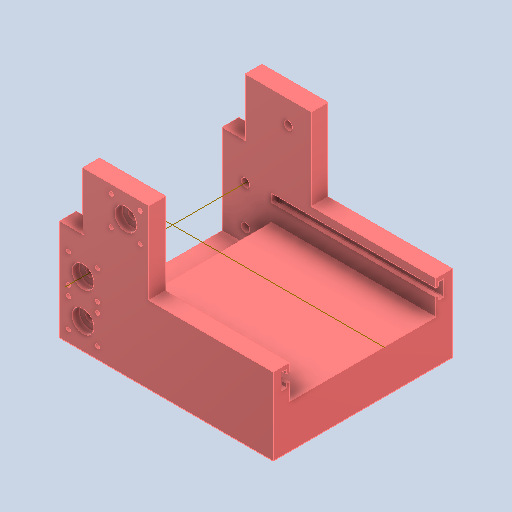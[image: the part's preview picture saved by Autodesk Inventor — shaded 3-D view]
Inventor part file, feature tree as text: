
AUTODESK INVENTOR PART (.ipt)
format: ipt  version: 2025 (Build 290162000, 162)  size: 441,344 bytes
history: native  units: mm
features: extrude x7, sketch x7, other x4, fillet x2, mirror x1, projected_geometry x1
ambient origin geometry x8: Origin, YZ Plane, XZ Plane, XY Plane, X Axis, Y Axis, Z Axis, Center Point
bodies: Body1 (feature_tree)
feature tree (22):
  parser-record x1  (decoder bookkeeping rows leaked as tree rows — omitted from the tree; the rows remain in map.json)
  other  "實體1"
  extrude  "擠出1"  Depth=120.0mm
  extrude  "擠出2"  Depth=335.0mm
  extrude  "擠出3"  Depth=255.0mm
  fillet  "圓角1"  Radius=525.0mm
  fillet  "圓角2"  Radius=585.5331mm
  extrude  "擠出7"  Depth=400.0mm
  extrude  "擠出4"  Depth=400.0mm
  extrude  "擠出5"  Depth=928.0mm
  extrude  "擠出6"  TaperAngle=0.0deg  [1 undecoded]
  mirror  "鏡射2"
  sketch  "草圖1"
  sketch  "草圖2"
  sketch  "草圖3"
  projected_geometry  "投影迴路1"
  sketch  "草圖4"
  sketch  "草圖5"
  sketch  "草圖6"
  sketch  "草圖7"
  other  "投影切割邊1"
  other  "投影切割邊3"
note: 1 required parameter value undecoded (feature->parameter linkage not recoverable at this tier; creation-order binding heuristic only, values carry confidence <= 0.55)
note: 1 file-system path scrubbed to <path> (originals preserved in map.json)
